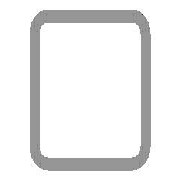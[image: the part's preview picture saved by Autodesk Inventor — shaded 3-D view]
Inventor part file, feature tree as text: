
AUTODESK INVENTOR PART (.ipt)
format: ipt  version: 2018 (Build 220112000, 112)  size: 150,016 bytes
history: native  units: mm (DEFAULTED — no unit token found)
features: other x4, sketch x4, extrude x2, plane x1
ambient origin geometry x8: Origin, YZ Plane, XZ Plane, XY Plane, X Axis, Y Axis, Z Axis, Center Point
bodies: Solid1 (feature_tree)
feature tree (11):
  other  "Tubolari horizontal 45"
  other  "Driven Length"
  other  "Piano iniziale"
  other  "Piano finale"
  extrude  "Corpo"  TaperAngle=0.0deg  [1 undecoded]
  extrude  "Estrusione2"  Depth=40.0mm
  sketch  "Schizzo"
  sketch  "Sketch3"  dims[d3=800.0mm d4=0.0mm]
  plane  "Work Plane3"
  sketch  "Sketch4"  dims[d7=4.0mm d9=40.0mm d11=40.0mm d12=2.0mm d13=-0.0mm d14=800.0mm d15=20.0mm d16=20.0mm d17=90.0deg d18=800.0mm d19=45.0deg d20=45.0deg d21=10.0mm d22=0.0mm]
  sketch  "Schizzo5"
note: 1 required parameter value undecoded (feature->parameter linkage not recoverable at this tier; creation-order binding heuristic only, values carry confidence <= 0.55)
